# Revit family: POJEMNIK NA RĘCZNIKI POJEDYNCZE MERIDA STELLA MINI
name_source: partatom
category: Modele ogólne
revit_build: Autodesk Revit 2015 (Build: 20140606_1530(x64)
units: mm (PartAtom-declared; Revit-internal decimal feet)

## types (3) — shared parameters
Autor = www.archispace.pl
Domyślna rzędna = 1200 mm
Grupa towarowa = PODAJNIKI RĘCZNIKÓW
Głębokość = 120 mm  [stored 0.393701 ft]
Karta techniczna produktu = https://sklep.merida.com.pl
Linia = MERIDA STELLA
Pojemność = 250 szt.
Producent = MERIDA SP. Z O.O.
Rodzaj montażu = naścienny
Szerokość = 255 mm  [stored 0.836614 ft]
Typ ręczników = składane ZZ
URL = www.merida.com.pl
Wielkość = MINI
Wysokość = 155 mm  [stored 0.50853 ft]

## per-type parameters (varying)
| type | Kolor | Materiał obudowa | Materiał obudowy | Model | Opis | Strona produktu |
| ASM201 | matowy | Merida_Stal_matowa | stal nierdzewna | Pojemnik na ręczniki składane MERIDA STELLA MINI, matowy | ASM201 Pojemnik na ręczniki papierowe składane MERIDA STELLA MINI. Pojemność 250 szt. Zamek bębenkowy, zlicowany z powierzchnią. Łączenia boków spawane i szlifowane. Zawiasy ukryte. | www.sklep.merida.com.pl/produkt/5677/pojemnik-na-reczniki-pojedyncze-merida-stella-mini-stal-matowa |
| ASP201 | polerowany | Merida_Stal_polerowana | stal nierdzewna | Pojemnik na ręczniki składane MERIDA STELLA MINI, polerowany | ASP201 Pojemnik na ręczniki papierowe składane MERIDA STELLA MINI. Pojemność 250 szt. Zamek bębenkowy, zlicowany z powierzchnią. Łączenia boków spawane i szlifowane. Zawiasy ukryte. | www.sklep.merida.com.pl/produkt/2743/pojemnik-na-reczniki-pojedyncze-merida-stella-mini-stal-polerowana |
| ASB201 | biały | Merida_biały_półmat | stal | Pojemnik na ręczniki składane MERIDA STELLA MINI, biały | ASBM201 Pojemnik na ręczniki papierowe składane MERIDA STELLA MINI. Malowany proszkowo na biało. Pojemność 250 szt. Zamek bębenkowy, zlicowany z powierzchnią. Łączenia boków spawane i szlifowane. Zawiasy ukryte. | www.sklep.merida.com.pl/produkt/6258/pojemnik-na-reczniki-pojedyncze-merida-stella-mini-bialy |

note: column(s) folded — value = type name in every type: Numer katalogowy

note: [stored X ft] marks values corroborated as IEEE doubles in the binary element streams (Revit-internal decimal feet)
